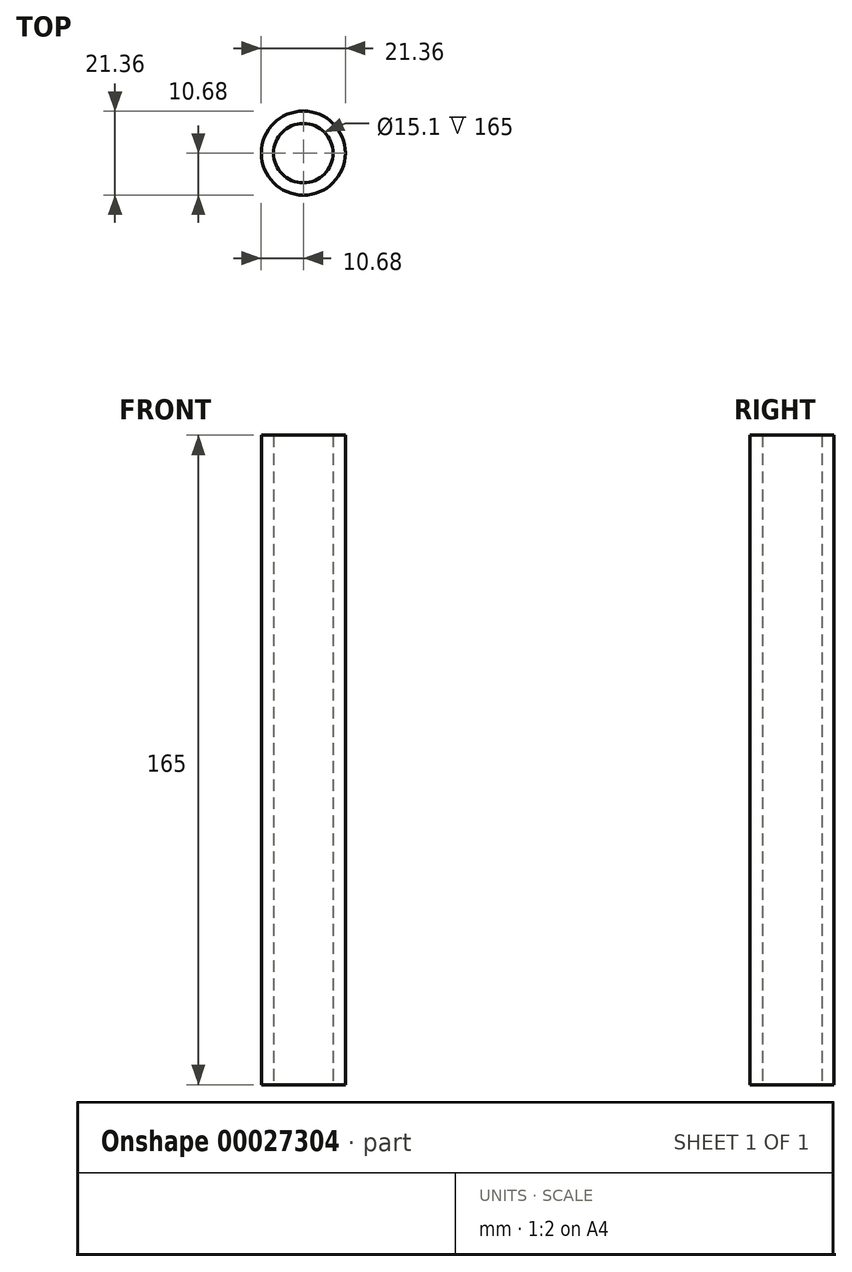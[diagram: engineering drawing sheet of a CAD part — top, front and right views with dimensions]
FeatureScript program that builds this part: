
annotation { "Feature Type Name" : "Feature", "Feature Type Description" : "" }
export const myFeature = defineFeature(function(context is Context, id is Id, definition is map)
    precondition{}
    {
        {
            var Q0;
            Q0=qCreatedBy(makeId("Top.planeOp"),FACE);
            var sketch = newSketch(context, id + "F0", { "sketchPlane" : qUnion([Q0])});
            skCircle(sketch, "E0", {"center": v(0, 0) * mm, "radius": 10.67 * mm});
            skCircle(sketch, "E1", {"center": v(0, 0) * mm, "radius": 7.55 * mm});
            skSolve(sketch);
        }
        {
            var Q0;
            Q0 = qSketchRegion(id + "F0", true);
            extrude(context, id + "F1", {"entities" : qUnion([Q0]), "depth" : 165 * mm});
        }
        {
            var Q0;
            Q0=makeQuery(id+"F1.opExtrude","CAP_FACE",FACE,{"disambiguationData":[OSD([sQuery(id+"F0.wireOp",EDGE,"E0"),sQuery(id+"F0.wireOp",EDGE,"E1")])],"isStart":false});
            var sketch = newSketch(context, id + "F2", { "sketchPlane" : qUnion([Q0])});
            skCircle(sketch, "E2", {"center": v(0, 0) * mm, "radius": 16.95 * mm});
            skSolve(sketch);
        }
        {
            var Q0;
            Q0 = qSketchRegion(id + "F2", true);
            extrude(context, id + "F3", {"entities" : qUnion([Q0]), "depth" : 3 * mm});
        }
        {
            var Q0;
            Q0=makeQuery(id+"F3.opExtrude","CAP_FACE",FACE,{"disambiguationData":[OSD([sQuery(id+"F2.wireOp",EDGE,"E2")])],"isStart":false});
            var sketch = newSketch(context, id + "F4", { "sketchPlane" : qUnion([Q0])});
            skCircle(sketch, "E3", {"center": v(0, 0) * mm, "radius": 7.45 * mm});
            skSolve(sketch);
        }
        {
            var Q0;
            Q0 = qSketchRegion(id + "F4", true);
            extrude(context, id + "F5", {"entities" : qUnion([Q0]), "operationType" : NewBodyOperationType.ADD, "oppositeDirection" : true, "depth" : 15 * mm});
        }
        {
            var Q0;
            Q0=makeQuery(id+"F5.opExtrude","CAP_EDGE",EDGE,{"disambiguationData":[OSD([sQuery(id+"F4.wireOp",EDGE,"E3")])],"isStart":false});
            chamfer(context, id + "F6", {"entities" : qUnion([Q0]), "width" : .5 * mm, "tangentPropagation" : true});
        }
        {
            var Q0;
            Q0=makeQuery(id+"F3.opExtrude","CAP_EDGE",EDGE,{"disambiguationData":[OSD([sQuery(id+"F2.wireOp",EDGE,"E2")])],"isStart":false});
            chamfer(context, id + "F7", {"entities" : qUnion([Q0]), "width" : 1 * mm, "tangentPropagation" : true});
        }
        {
            var Q0;
            Q0=qCreatedBy(makeId("Front.planeOp"),FACE);
            var sketch = newSketch(context, id + "F8", { "sketchPlane" : qUnion([Q0])});
            skLineSegment(sketch, "E4.bottom", {"start": v(-7.47, 159.4) * mm, "end": v(-5.72, 159.4) * mm});
            skLineSegment(sketch, "E4.top", {"start": v(-7.47, 157) * mm, "end": v(-5.72, 157) * mm});
            skLineSegment(sketch, "E4.right", {"start": v(-5.72, 159.4) * mm, "end": v(-5.72, 157) * mm});
            skLineSegment(sketch, "E5", {"start": v(0, 0) * mm, "end": v(0, 184.46) * mm, "construction": true});
            skLineSegment(sketch, "E6", {"start": v(-7.47, 159.4) * mm, "end": v(-7.47, 157) * mm});
            skSolve(sketch);
        }
        {
            var Q0;
            Q0 = qSketchRegion(id + "F8", true);
            var Q1;
            Q1=sQuery(id+"F8.wireOp",EDGE,"E5");
            revolve(context, id + "F9", {"operationType" : NewBodyOperationType.REMOVE, "entities" : qUnion([Q0]), "axis" : qUnion([Q1]), "revolveType" : RevolveType.FULL, "oppositeDirection" : true});
        }
        {
            var Q0;
            Q0=makeQuery(id+"F9.boolean.opBoolean","COPY",EDGE,{"derivedFrom":makeQuery(id+"F9.opRevolve","SWEPT_EDGE",EDGE,{"disambiguationData":[OSD([sQuery(id+"F8.wireOp",EDGE,"E4.bottom"),sQuery(id+"F8.wireOp",EDGE,"E4.right")])]})});
            var Q1;
            Q1=makeQuery(id+"F9.boolean.opBoolean","COPY",EDGE,{"derivedFrom":makeQuery(id+"F9.opRevolve","SWEPT_EDGE",EDGE,{"disambiguationData":[OSD([sQuery(id+"F8.wireOp",EDGE,"E4.top"),sQuery(id+"F8.wireOp",EDGE,"E4.right")])]})});
            fillet(context, id + "F10", {"entities" : qUnion([Q0, Q1]), "radius" : 1 * mm, "tangentPropagation" : true, "allowEdgeOverflow" : false});
        }
        {
            var Q0;
            Q0=makeQuery(id+"F9.boolean.opBoolean","INTERSECT",EDGE,{"derivedFrom":[makeQuery(id+"F5.opExtrude","SWEPT_FACE",FACE,{"disambiguationData":[OSD([sQuery(id+"F4.wireOp",EDGE,"E3")])]}),makeQuery(id+"F9.opRevolve","SWEPT_FACE",FACE,{"disambiguationData":[OSD([sQuery(id+"F8.wireOp",EDGE,"E4.top")])]})]});
            var Q1;
            Q1=makeQuery(id+"F9.boolean.opBoolean","INTERSECT",EDGE,{"derivedFrom":[makeQuery(id+"F5.opExtrude","SWEPT_FACE",FACE,{"disambiguationData":[OSD([sQuery(id+"F4.wireOp",EDGE,"E3")])]}),makeQuery(id+"F9.opRevolve","SWEPT_FACE",FACE,{"disambiguationData":[OSD([sQuery(id+"F8.wireOp",EDGE,"E4.bottom")])]})]});
            fillet(context, id + "F11", {"entities" : qUnion([Q0, Q1]), "radius" : .5 * mm, "tangentPropagation" : true, "allowEdgeOverflow" : false});
        }
        {
            var Q0;
            Q0=makeQuery(id+"F3.opExtrude","SWEPT_BODY",BODY,{"disambiguationData":[OSD([sQuery(id+"F2.wireOp",EDGE,"E2")])]});
            deleteBodies(context, id + "F12", {"entities" : qUnion([Q0])});
        }
    });
